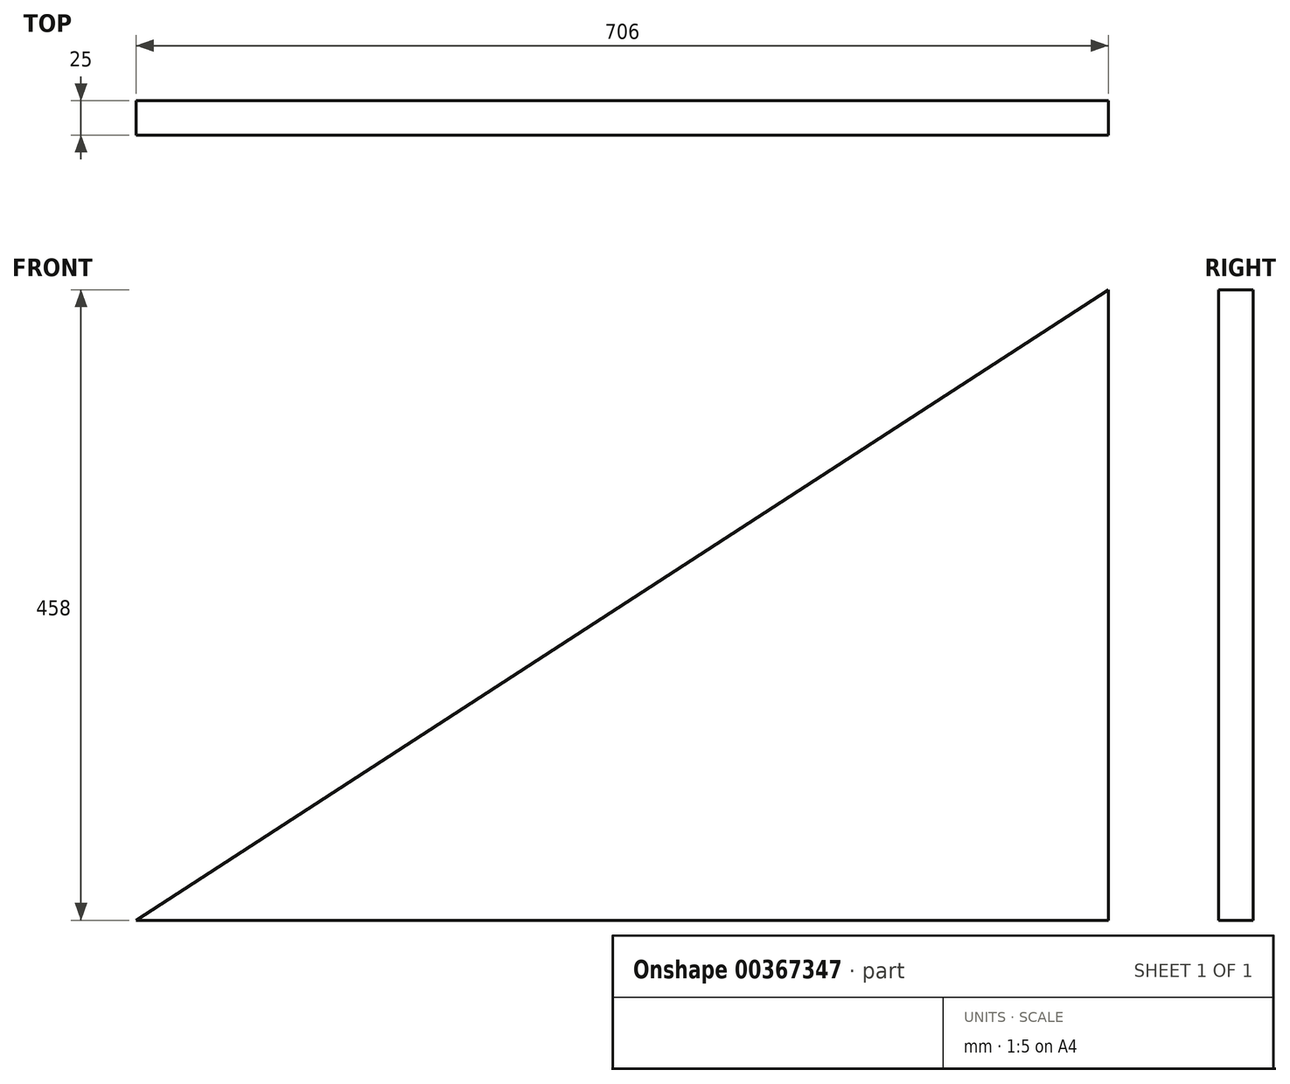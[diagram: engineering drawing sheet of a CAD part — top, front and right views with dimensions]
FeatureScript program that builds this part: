
annotation { "Feature Type Name" : "Feature", "Feature Type Description" : "" }
export const myFeature = defineFeature(function(context is Context, id is Id, definition is map)
    precondition{}
    {
        {
            var Q0;
            Q0=qCreatedBy(makeId("Front.planeOp"),FACE);
            var sketch = newSketch(context, id + "F0", { "sketchPlane" : qUnion([Q0])});
            skLineSegment(sketch, "E0", {"start": v(0, 0) * mm, "end": v(706, 0) * mm});
            skLineSegment(sketch, "E1", {"start": v(706, 0) * mm, "end": v(706, 458) * mm});
            skLineSegment(sketch, "E2", {"start": v(706, 458) * mm, "end": v(0, 0) * mm});
            skSolve(sketch);
        }
        {
            var Q0;
            Q0 = qSketchRegion(id + "F0", true);
            extrude(context, id + "F1", {"entities" : qUnion([Q0]), "depth" : 25 * mm});
        }
    });
